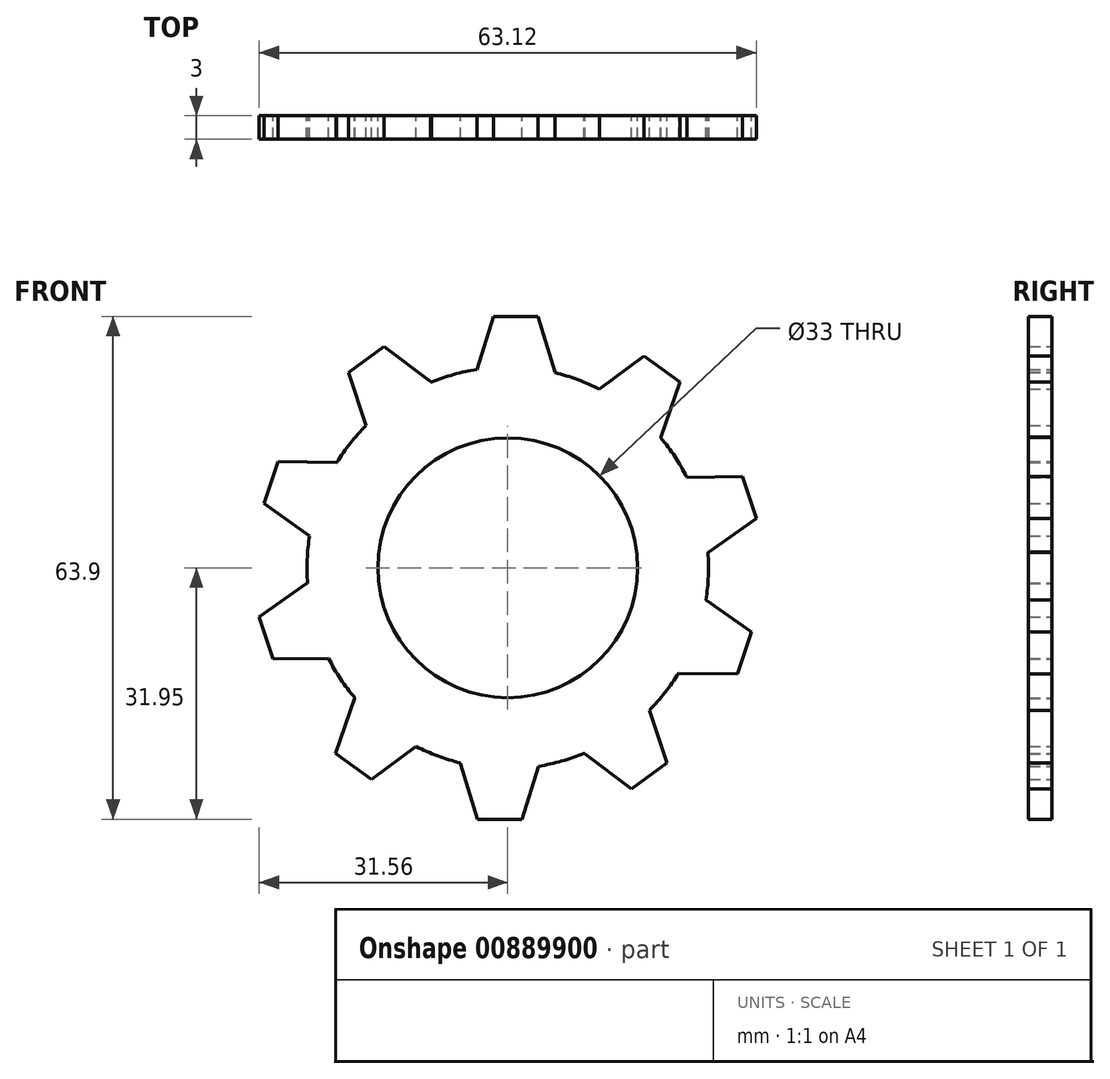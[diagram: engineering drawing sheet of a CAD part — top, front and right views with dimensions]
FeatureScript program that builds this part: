
annotation { "Feature Type Name" : "Feature", "Feature Type Description" : "" }
export const myFeature = defineFeature(function(context is Context, id is Id, definition is map)
    precondition{}
    {
        {
            var Q0;
            Q0=qCreatedBy(makeId("Front.planeOp"),FACE);
            var sketch = newSketch(context, id + "F0", { "sketchPlane" : qUnion([Q0])});
            skArc(sketch, "E0", {"start": v(5, 7.08) * mm, "mid": v(5, 7.14) * mm, "end": v(5, 7.2) * mm});
            skLineSegment(sketch, "E1", {"start": v(-5, 7.2) * mm, "end": v(-2.81, 14.25) * mm});
            skLineSegment(sketch, "E2.MirrorCS", {"start": v(5, 7.2) * mm, "end": v(2.81, 14.25) * mm});
            skLineSegment(sketch, "E3", {"start": v(-2.81, 14.25) * mm, "end": v(2.81, 14.25) * mm});
            skArc(sketch, "E4.1.0", {"start": v(-10.71, 5.88) * mm, "mid": v(-10.75, 5.92) * mm, "end": v(-10.78, 5.97) * mm});
            skLineSegment(sketch, "E4.1.1", {"start": v(-10.78, 5.97) * mm, "end": v(-16.7, 10.39) * mm});
            skLineSegment(sketch, "E4.1.2", {"start": v(-21.24, 7.08) * mm, "end": v(-16.7, 10.39) * mm});
            skLineSegment(sketch, "E4.1.3", {"start": v(-18.87, 0.1) * mm, "end": v(-21.24, 7.08) * mm});
            skArc(sketch, "E4.2.0", {"start": v(-22.72, -4.34) * mm, "mid": v(-22.77, -4.32) * mm, "end": v(-22.83, -4.3) * mm});
            skLineSegment(sketch, "E4.2.1", {"start": v(-22.83, -4.3) * mm, "end": v(-30.2, -4.2) * mm});
            skLineSegment(sketch, "E4.2.2", {"start": v(-31.94, -9.55) * mm, "end": v(-30.2, -4.2) * mm});
            skLineSegment(sketch, "E4.2.3", {"start": v(-25.92, -13.8) * mm, "end": v(-31.94, -9.55) * mm});
            skArc(sketch, "E4.3.0", {"start": v(-26.43, -19.65) * mm, "mid": v(-26.48, -19.67) * mm, "end": v(-26.54, -19.69) * mm});
            skLineSegment(sketch, "E4.3.1", {"start": v(-26.54, -19.69) * mm, "end": v(-32.56, -23.95) * mm});
            skLineSegment(sketch, "E4.3.2", {"start": v(-30.82, -29.3) * mm, "end": v(-32.56, -23.95) * mm});
            skLineSegment(sketch, "E4.3.3", {"start": v(-23.45, -29.2) * mm, "end": v(-30.82, -29.3) * mm});
            skArc(sketch, "E4.4.0", {"start": v(-20.42, -34.23) * mm, "mid": v(-20.46, -34.27) * mm, "end": v(-20.49, -34.32) * mm});
            skLineSegment(sketch, "E4.4.1", {"start": v(-20.49, -34.32) * mm, "end": v(-22.86, -41.3) * mm});
            skLineSegment(sketch, "E4.4.2", {"start": v(-18.31, -44.6) * mm, "end": v(-22.86, -41.3) * mm});
            skLineSegment(sketch, "E4.4.3", {"start": v(-12.4, -40.2) * mm, "end": v(-18.31, -44.6) * mm});
            skArc(sketch, "E4.5.0", {"start": v(-7, -42.48) * mm, "mid": v(-7, -42.54) * mm, "end": v(-7, -42.6) * mm});
            skLineSegment(sketch, "E4.5.1", {"start": v(-7, -42.6) * mm, "end": v(-4.81, -49.65) * mm});
            skLineSegment(sketch, "E4.5.2", {"start": v(0.81, -49.65) * mm, "end": v(-4.81, -49.65) * mm});
            skLineSegment(sketch, "E4.5.3", {"start": v(3, -42.6) * mm, "end": v(0.81, -49.65) * mm});
            skArc(sketch, "E4.6.0", {"start": v(8.71, -41.28) * mm, "mid": v(8.75, -41.32) * mm, "end": v(8.78, -41.37) * mm});
            skLineSegment(sketch, "E4.6.1", {"start": v(8.78, -41.37) * mm, "end": v(14.7, -45.79) * mm});
            skLineSegment(sketch, "E4.6.2", {"start": v(19.24, -42.48) * mm, "end": v(14.7, -45.79) * mm});
            skLineSegment(sketch, "E4.6.3", {"start": v(16.87, -35.5) * mm, "end": v(19.24, -42.48) * mm});
            skArc(sketch, "E4.7.0", {"start": v(20.72, -31.06) * mm, "mid": v(20.77, -31.08) * mm, "end": v(20.83, -31.1) * mm});
            skLineSegment(sketch, "E4.7.1", {"start": v(20.83, -31.1) * mm, "end": v(28.2, -31.2) * mm});
            skLineSegment(sketch, "E4.7.2", {"start": v(29.94, -25.85) * mm, "end": v(28.2, -31.2) * mm});
            skLineSegment(sketch, "E4.7.3", {"start": v(23.92, -21.6) * mm, "end": v(29.94, -25.85) * mm});
            skArc(sketch, "E4.8.0", {"start": v(24.43, -15.75) * mm, "mid": v(24.48, -15.73) * mm, "end": v(24.54, -15.71) * mm});
            skLineSegment(sketch, "E4.8.1", {"start": v(24.54, -15.71) * mm, "end": v(30.56, -11.45) * mm});
            skLineSegment(sketch, "E4.8.2", {"start": v(28.82, -6.1) * mm, "end": v(30.56, -11.45) * mm});
            skLineSegment(sketch, "E4.8.3", {"start": v(21.45, -6.2) * mm, "end": v(28.82, -6.1) * mm});
            skArc(sketch, "E4.9.0", {"start": v(18.42, -1.17) * mm, "mid": v(18.46, -1.13) * mm, "end": v(18.49, -1.08) * mm});
            skLineSegment(sketch, "E4.9.1", {"start": v(18.49, -1.08) * mm, "end": v(20.86, 5.9) * mm});
            skLineSegment(sketch, "E4.9.2", {"start": v(16.31, 9.2) * mm, "end": v(20.86, 5.9) * mm});
            skLineSegment(sketch, "E4.9.3", {"start": v(10.4, 4.8) * mm, "end": v(16.31, 9.2) * mm});
            skPoint(sketch, "E4.center", {"position": v(-1, -17.7) * mm});
            skArc(sketch, "E5", {"start": v(-18.97, 0.39) * mm, "mid": v(-20.99, -1.86) * mm, "end": v(-22.72, -4.34) * mm});
            skArc(sketch, "E6.trimOffspring", {"start": v(-26.17, -13.63) * mm, "mid": v(-26.48, -16.63) * mm, "end": v(-26.43, -19.65) * mm});
            skArc(sketch, "E7.trimOffspring", {"start": v(-23.76, -29.2) * mm, "mid": v(-22.24, -31.81) * mm, "end": v(-20.42, -34.23) * mm});
            skArc(sketch, "E8.trimOffspring", {"start": v(-12.65, -40.38) * mm, "mid": v(-9.89, -41.6) * mm, "end": v(-7, -42.48) * mm});
            skArc(sketch, "E9.trimOffspring", {"start": v(2.9, -42.9) * mm, "mid": v(5.86, -42.26) * mm, "end": v(8.71, -41.28) * mm});
            skArc(sketch, "E10.trimOffspring", {"start": v(16.97, -35.79) * mm, "mid": v(18.99, -33.54) * mm, "end": v(20.72, -31.06) * mm});
            skArc(sketch, "E11.trimOffspring", {"start": v(24.17, -21.77) * mm, "mid": v(24.48, -18.77) * mm, "end": v(24.43, -15.75) * mm});
            skArc(sketch, "E12.trimOffspring", {"start": v(21.76, -6.2) * mm, "mid": v(20.24, -3.59) * mm, "end": v(18.42, -1.17) * mm});
            skArc(sketch, "E13.trimOffspring", {"start": v(10.65, 4.98) * mm, "mid": v(7.89, 6.2) * mm, "end": v(5, 7.08) * mm});
            skArc(sketch, "E14.trimOffspring", {"start": v(-4.9, 7.5) * mm, "mid": v(-7.86, 6.86) * mm, "end": v(-10.71, 5.88) * mm});
            skCircle(sketch, "E15", {"center": v(-1, -17.7) * mm, "radius": 16.5 * mm});
            skSolve(sketch);
        }
        {
            var Q0;
            Q0 = qSketchRegion(id + "F0", true);
            extrude(context, id + "F1", {"entities" : qUnion([Q0]), "depth" : 3 * mm, "offsetDistance" : 25 * mm});
        }
        {
            var Q0;
            Q0 = qSketchRegion(id + "F0", true);
            extrude(context, id + "F2", {"entities" : qUnion([Q0]), "operationType" : NewBodyOperationType.ADD, "depth" : 3 * mm, "offsetDistance" : 25 * mm});
        }
    });
